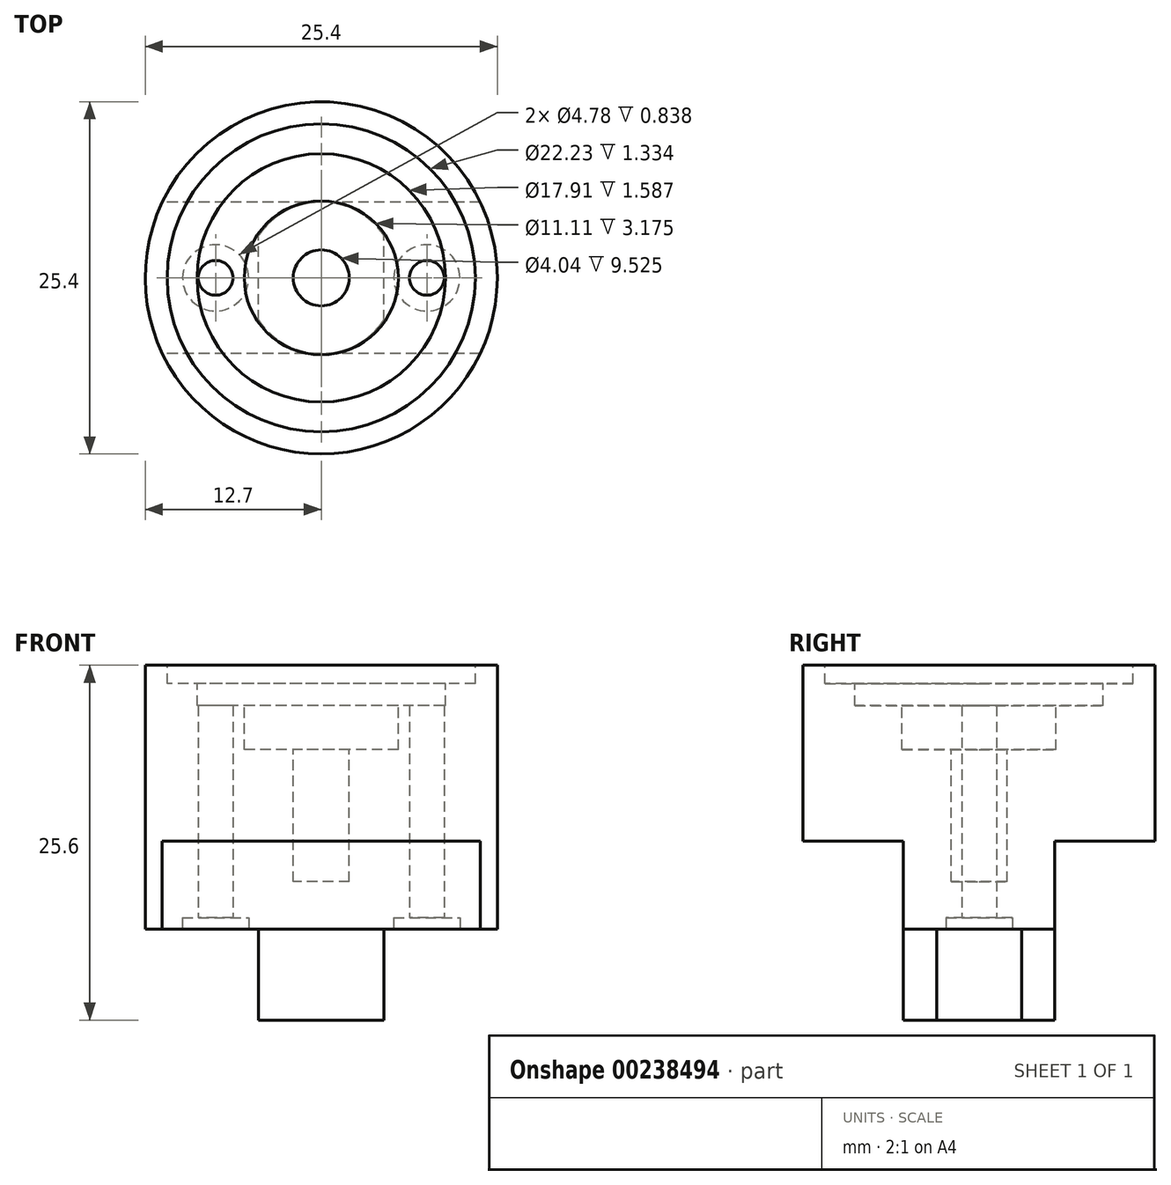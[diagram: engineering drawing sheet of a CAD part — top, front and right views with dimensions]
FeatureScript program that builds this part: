
annotation { "Feature Type Name" : "Feature", "Feature Type Description" : "" }
export const myFeature = defineFeature(function(context is Context, id is Id, definition is map)
    precondition{}
    {
        {
            var Q0;
            Q0=qCreatedBy(makeId("Top.planeOp"),FACE);
            var sketch = newSketch(context, id + "F0", { "sketchPlane" : qUnion([Q0])});
            skCircle(sketch, "E0", {"center": v(0, 0) * mm, "radius": 12.7 * mm});
            skCircle(sketch, "E1", {"center": v(-7.62, 0) * mm, "radius": 1.25 * mm});
            skCircle(sketch, "E2.1.0", {"center": v(7.62, 0) * mm, "radius": 1.25 * mm});
            skSolve(sketch);
        }
        {
            var Q0;
            Q0 = qSketchRegion(id + "F0", true);
            extrude(context, id + "F1", {"entities" : qUnion([Q0]), "depth" : 19.05 * mm});
        }
        {
            var Q0;
            Q0=makeQuery(id+"F1.opExtrude","CAP_FACE",FACE,{"disambiguationData":[OSD([sQuery(id+"F0.wireOp",EDGE,"E0"),sQuery(id+"F0.wireOp",EDGE,"E1"),sQuery(id+"F0.wireOp",EDGE,"E2.1.0")])],"isStart":false});
            var sketch = newSketch(context, id + "F2", { "sketchPlane" : qUnion([Q0])});
            skCircle(sketch, "E3", {"center": v(0, 0) * mm, "radius": 11.11 * mm});
            skSolve(sketch);
        }
        {
            var Q0;
            Q0 = qSketchRegion(id + "F2", true);
            extrude(context, id + "F3", {"entities" : qUnion([Q0]), "operationType" : NewBodyOperationType.REMOVE, "oppositeDirection" : true, "depth" : 1.33 * mm});
        }
        {
            var Q0;
            Q0=makeQuery(id+"F3.boolean.opBoolean","COPY",FACE,{"derivedFrom":makeQuery(id+"F3.opExtrude","CAP_FACE",FACE,{"disambiguationData":[OSD([sQuery(id+"F2.wireOp",EDGE,"E3")])],"isStart":false})});
            var sketch = newSketch(context, id + "F4", { "sketchPlane" : qUnion([Q0])});
            skCircle(sketch, "E4", {"center": v(0, 0) * mm, "radius": 8.95 * mm});
            skSolve(sketch);
        }
        {
            var Q0;
            Q0 = qSketchRegion(id + "F4", true);
            extrude(context, id + "F5", {"entities" : qUnion([Q0]), "operationType" : NewBodyOperationType.REMOVE, "oppositeDirection" : true, "depth" : 1.59 * mm});
        }
        {
            var Q0;
            Q0=makeQuery(id+"F1.opExtrude","CAP_FACE",FACE,{"disambiguationData":[OSD([sQuery(id+"F0.wireOp",EDGE,"E0"),sQuery(id+"F0.wireOp",EDGE,"E1"),sQuery(id+"F0.wireOp",EDGE,"E2.1.0")])],"isStart":true});
            var sketch = newSketch(context, id + "F6", { "sketchPlane" : qUnion([Q0])});
            skCircle(sketch, "E5", {"center": v(-7.62, 0) * mm, "radius": 2.39 * mm});
            skCircle(sketch, "E6.1.0", {"center": v(7.62, 0) * mm, "radius": 2.39 * mm});
            skPoint(sketch, "E6.center", {"position": v(0, 0) * mm});
            skSolve(sketch);
        }
        {
            var Q0;
            Q0=makeQuery(id+"F6.imprint","IMPRINT",FACE,{"disambiguationData":[TD([[makeQuery(id+"F6.imprint","IMPRINT",EDGE,{"derivedFrom":sQuery(id+"F6.wireOp",EDGE,"E5")}),1.0]])]});
            var Q1;
            Q1=makeQuery(id+"F6.imprint","IMPRINT",FACE,{"disambiguationData":[TD([[makeQuery(id+"F6.imprint","IMPRINT",EDGE,{"derivedFrom":sQuery(id+"F6.wireOp",EDGE,"E6.1.0")}),1.0]])]});
            extrude(context, id + "F7", {"entities" : qUnion([Q0, Q1]), "operationType" : NewBodyOperationType.REMOVE, "oppositeDirection" : true, "depth" : 0.84 * mm});
        }
        {
            var Q0;
            Q0=makeQuery(id+"F1.opExtrude","CAP_FACE",FACE,{"disambiguationData":[OSD([sQuery(id+"F0.wireOp",EDGE,"E0"),sQuery(id+"F0.wireOp",EDGE,"E1"),sQuery(id+"F0.wireOp",EDGE,"E2.1.0")])],"isStart":true});
            var sketch = newSketch(context, id + "F8", { "sketchPlane" : qUnion([Q0])});
            skArc(sketch, "E7", {"start": v(-4.52, -3.06) * mm, "mid": v(0, -5.46) * mm, "end": v(4.52, -3.06) * mm});
            skLineSegment(sketch, "E8", {"start": v(-4.52, 3.06) * mm, "end": v(-4.52, -3.06) * mm});
            skLineSegment(sketch, "E9.MirrorCS", {"start": v(4.52, 3.06) * mm, "end": v(4.52, -3.06) * mm});
            skArc(sketch, "E10.trimOffspring", {"start": v(4.52, 3.06) * mm, "mid": v(0, 5.46) * mm, "end": v(-4.52, 3.06) * mm});
            skSolve(sketch);
        }
        {
            var Q0;
            Q0 = qSketchRegion(id + "F8", true);
            extrude(context, id + "F9", {"entities" : qUnion([Q0]), "operationType" : NewBodyOperationType.ADD, "depth" : 6.55 * mm});
        }
        {
            var Q0;
            Q0=makeQuery(id+"F5.boolean.opBoolean","COPY",FACE,{"derivedFrom":makeQuery(id+"F5.opExtrude","CAP_FACE",FACE,{"disambiguationData":[OSD([sQuery(id+"F4.wireOp",EDGE,"E4")])],"isStart":false})});
            var sketch = newSketch(context, id + "F10", { "sketchPlane" : qUnion([Q0])});
            skCircle(sketch, "E11", {"center": v(0, 0) * mm, "radius": 2.02 * mm});
            skSolve(sketch);
        }
        {
            var Q0;
            Q0 = qSketchRegion(id + "F10", true);
            extrude(context, id + "F11", {"entities" : qUnion([Q0]), "operationType" : NewBodyOperationType.REMOVE, "oppositeDirection" : true, "depth" : 12.7 * mm});
        }
        {
            var Q0;
            Q0=makeQuery(id+"F5.boolean.opBoolean","COPY",FACE,{"derivedFrom":makeQuery(id+"F5.opExtrude","CAP_FACE",FACE,{"disambiguationData":[OSD([sQuery(id+"F4.wireOp",EDGE,"E4")])],"isStart":false})});
            var sketch = newSketch(context, id + "F12", { "sketchPlane" : qUnion([Q0])});
            skCircle(sketch, "E12", {"center": v(0, 0) * mm, "radius": 5.56 * mm});
            skSolve(sketch);
        }
        {
            var Q0;
            Q0 = qSketchRegion(id + "F12", true);
            extrude(context, id + "F13", {"entities" : qUnion([Q0]), "operationType" : NewBodyOperationType.REMOVE, "oppositeDirection" : true, "depth" : 3.17 * mm});
        }
        {
            var Q0;
            Q0=qCreatedBy(makeId("Front.planeOp"),FACE);
            cPlane(context, id + "F14", {"entities" : qUnion([Q0]), "cplaneType" : CPlaneType.OFFSET, "offset" : 5.46 * mm, "width" : 152.4 * mm, "height" : 152.4 * mm});
        }
        {
            var Q0;
            Q0=qCreatedBy(id+"F14.planeOp",FACE);
            var sketch = newSketch(context, id + "F15", { "sketchPlane" : qUnion([Q0])});
            skLineSegment(sketch, "E13.bottom", {"start": v(15.7, 0) * mm, "end": v(-16.42, 0) * mm});
            skLineSegment(sketch, "E13.top", {"start": v(15.7, 6.35) * mm, "end": v(-16.42, 6.35) * mm});
            skLineSegment(sketch, "E13.left", {"start": v(15.7, 0) * mm, "end": v(15.7, 6.35) * mm});
            skLineSegment(sketch, "E13.right", {"start": v(-16.42, 0) * mm, "end": v(-16.42, 6.35) * mm});
            skSolve(sketch);
        }
        {
            var Q0;
            Q0 = qSketchRegion(id + "F15", true);
            extrude(context, id + "F16", {"entities" : qUnion([Q0]), "operationType" : NewBodyOperationType.REMOVE, "depth" : 25.4 * mm});
        }
        {
            var Q0;
            Q0=qCreatedBy(makeId("Front.planeOp"),FACE);
            cPlane(context, id + "F17", {"entities" : qUnion([Q0]), "cplaneType" : CPlaneType.OFFSET, "offset" : 5.46 * mm, "oppositeDirection" : true, "width" : 152.4 * mm, "height" : 152.4 * mm});
        }
        {
            var Q0;
            Q0=qCreatedBy(id+"F17.planeOp",FACE);
            var sketch = newSketch(context, id + "F18", { "sketchPlane" : qUnion([Q0])});
            skLineSegment(sketch, "E14.bottom", {"start": v(13.93, 0) * mm, "end": v(-15.7, 0) * mm});
            skLineSegment(sketch, "E14.top", {"start": v(13.93, 6.35) * mm, "end": v(-15.7, 6.35) * mm});
            skLineSegment(sketch, "E14.left", {"start": v(13.93, 0) * mm, "end": v(13.93, 6.35) * mm});
            skLineSegment(sketch, "E14.right", {"start": v(-15.7, 0) * mm, "end": v(-15.7, 6.35) * mm});
            skSolve(sketch);
        }
        {
            var Q0;
            Q0 = qSketchRegion(id + "F18", true);
            extrude(context, id + "F19", {"entities" : qUnion([Q0]), "operationType" : NewBodyOperationType.REMOVE, "oppositeDirection" : true, "depth" : 25.4 * mm});
        }
    });
